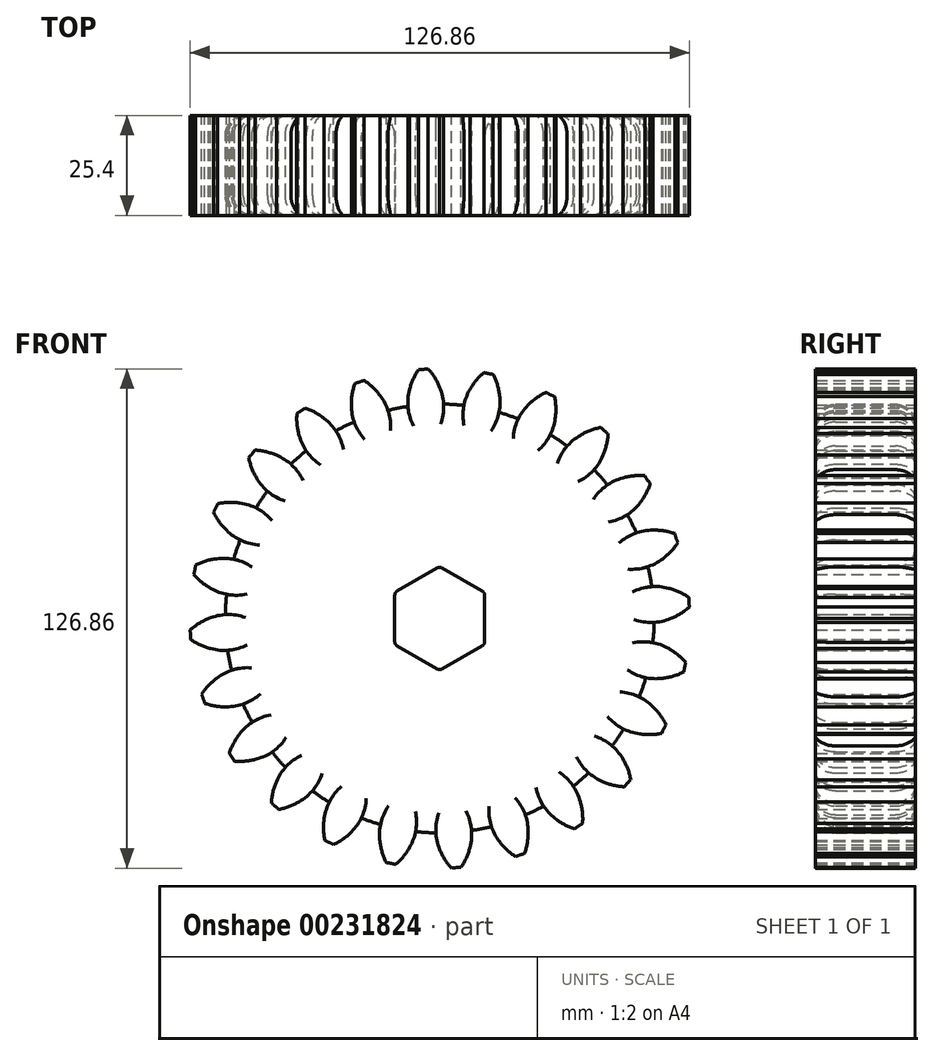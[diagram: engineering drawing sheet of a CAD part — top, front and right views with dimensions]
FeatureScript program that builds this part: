
annotation { "Feature Type Name" : "Feature", "Feature Type Description" : "" }
export const myFeature = defineFeature(function(context is Context, id is Id, definition is map)
    precondition{}
    {
        {
            var Q0;
            Q0=qCreatedBy(makeId("Front.planeOp"),FACE);
            var sketch = newSketch(context, id + "F0", { "sketchPlane" : qUnion([Q0])});
            skCircle(sketch, "E0", {"center": v(0, 0) * mm, "radius": 63.5 * mm, "construction": true});
            skCircle(sketch, "E1", {"center": v(0, 0) * mm, "radius": 58.67 * mm, "construction": true});
            skCircle(sketch, "E2", {"center": v(0, 0) * mm, "radius": 53.72 * mm});
            skLineSegment(sketch, "E3", {"start": v(0, 0) * mm, "end": v(0, 146.74) * mm, "construction": true});
            skLineSegment(sketch, "E4", {"start": v(0, 0) * mm, "end": v(-9.9, 151.07) * mm, "construction": true});
            skLineSegment(sketch, "E5", {"start": v(0, 58.67) * mm, "end": v(-143.25, 58.67) * mm, "construction": true});
            skLineSegment(sketch, "E6", {"start": v(0, 58.67) * mm, "end": v(-135.03, 9.53) * mm, "construction": true});
            skCircle(sketch, "E7", {"center": v(0, 0) * mm, "radius": 55.14 * mm, "construction": true});
            skCircle(sketch, "E8", {"center": v(0, 58.67) * mm, "radius": 14.6 * mm, "construction": true});
            skCircle(sketch, "E9", {"center": v(-13.63, 53.42) * mm, "radius": 14.64 * mm, "construction": true});
            skArc(sketch, "E10", {"start": v(0, 58.67) * mm, "mid": v(-1.26, 61.19) * mm, "end": v(-2.95, 63.43) * mm});
            skArc(sketch, "E11", {"start": v(1, 53.71) * mm, "mid": v(0.75, 56.24) * mm, "end": v(0, 58.67) * mm});
            skArc(sketch, "E12.MirrorCS", {"start": v(-7.66, 58.17) * mm, "mid": v(-6.74, 60.83) * mm, "end": v(-5.36, 63.27) * mm});
            skArc(sketch, "E13", {"start": v(-5.36, 63.27) * mm, "mid": v(-4.15, 63.3) * mm, "end": v(-2.95, 63.43) * mm});
            skArc(sketch, "E14.MirrorCS", {"start": v(-8, 53.12) * mm, "mid": v(-8.08, 55.66) * mm, "end": v(-7.66, 58.17) * mm});
            skSolve(sketch);
        }
        {
            var Q0;
            {var subQ0=sQuery(id+"F0.wireOp",EDGE,"E2");var subQ1=makeQuery(id+"F0.imprint","INTERSECT",VERTEX,{"derivedFrom":[subQ0,sQuery(id+"F0.wireOp",EDGE,"E11")]});Q0=makeQuery(id+"F0.imprint","IMPRINT",FACE,{"disambiguationData":[TD([[makeQuery(id+"F0.imprint","IMPRINT",EDGE,{"disambiguationData":[TD([[subQ1,-1.0]])],"derivedFrom":subQ0}),1.0]])]});}
            var Q1;
            Q1=makeQuery(id+"F0.imprint","IMPRINT",FACE,{"disambiguationData":[TD([[makeQuery(id+"F0.imprint","IMPRINT",EDGE,{"derivedFrom":sQuery(id+"F0.wireOp",EDGE,"E10")}),1.0]])]});
            extrude(context, id + "F1", {"entities" : qUnion([Q0, Q1]), "depth" : 25.4 * mm});
        }
        {
            var Q0;
            Q0=makeQuery(id+"F1.opExtrude","SWEPT_BODY",BODY,{"disambiguationData":[OSD([sQuery(id+"F0.wireOp",EDGE,"E2"),sQuery(id+"F0.wireOp",EDGE,"E10"),sQuery(id+"F0.wireOp",EDGE,"E11"),sQuery(id+"F0.wireOp",EDGE,"E12.MirrorCS"),sQuery(id+"F0.wireOp",EDGE,"E13"),sQuery(id+"F0.wireOp",EDGE,"E14.MirrorCS")])]});
            var Q1;
            Q1=makeQuery(id+"F1.opExtrude","SWEPT_FACE",FACE,{"disambiguationData":[OSD([sQuery(id+"F0.wireOp",EDGE,"E2")])]});
            circularPattern(context, id + "F2", {"entities" : qUnion([Q0]), "axis" : qUnion([Q1]), "angle" : 15 * degree, "instanceCount" : 24});
        }
        {
            var Q0;
            Q0=makeQuery(id+"F2.opPattern","COPY",FACE,{"derivedFrom":makeQuery(id+"F1.opExtrude","CAP_FACE",FACE,{"disambiguationData":[OSD([sQuery(id+"F0.wireOp",EDGE,"E2"),sQuery(id+"F0.wireOp",EDGE,"E10"),sQuery(id+"F0.wireOp",EDGE,"E11"),sQuery(id+"F0.wireOp",EDGE,"E12.MirrorCS"),sQuery(id+"F0.wireOp",EDGE,"E13"),sQuery(id+"F0.wireOp",EDGE,"E14.MirrorCS")])],"isStart":true}),"instanceName":"12"});
            var sketch = newSketch(context, id + "F3", { "sketchPlane" : qUnion([Q0])});
            skCircle(sketch, "E15", {"center": v(0, 0) * mm, "radius": 54.48 * mm});
            skSolve(sketch);
        }
        {
            var Q0;
            Q0 = qSketchRegion(id + "F3", true);
            extrude(context, id + "F4", {"entities" : qUnion([Q0]), "operationType" : NewBodyOperationType.ADD, "oppositeDirection" : true, "depth" : 25.4 * mm});
        }
        {
            var Q0;
            {var subQ0=makeQuery(id+"F1.opExtrude","CAP_FACE",FACE,{"disambiguationData":[OSD([sQuery(id+"F0.wireOp",EDGE,"E2"),sQuery(id+"F0.wireOp",EDGE,"E10"),sQuery(id+"F0.wireOp",EDGE,"E11"),sQuery(id+"F0.wireOp",EDGE,"E12.MirrorCS"),sQuery(id+"F0.wireOp",EDGE,"E13"),sQuery(id+"F0.wireOp",EDGE,"E14.MirrorCS")])],"isStart":false});Q0=makeQuery(id+"F4.boolean.opBoolean","MERGE",FACE,{"derivedFrom":[subQ0,makeQuery(id+"F2.opPattern","COPY",FACE,{"derivedFrom":subQ0,"instanceName":"1"}),makeQuery(id+"F2.opPattern","COPY",FACE,{"derivedFrom":subQ0,"instanceName":"2"}),makeQuery(id+"F2.opPattern","COPY",FACE,{"derivedFrom":subQ0,"instanceName":"3"}),makeQuery(id+"F2.opPattern","COPY",FACE,{"derivedFrom":subQ0,"instanceName":"4"}),makeQuery(id+"F2.opPattern","COPY",FACE,{"derivedFrom":subQ0,"instanceName":"5"}),makeQuery(id+"F2.opPattern","COPY",FACE,{"derivedFrom":subQ0,"instanceName":"6"}),makeQuery(id+"F2.opPattern","COPY",FACE,{"derivedFrom":subQ0,"instanceName":"7"}),makeQuery(id+"F2.opPattern","COPY",FACE,{"derivedFrom":subQ0,"instanceName":"8"}),makeQuery(id+"F2.opPattern","COPY",FACE,{"derivedFrom":subQ0,"instanceName":"9"}),makeQuery(id+"F2.opPattern","COPY",FACE,{"derivedFrom":subQ0,"instanceName":"10"}),makeQuery(id+"F2.opPattern","COPY",FACE,{"derivedFrom":subQ0,"instanceName":"11"}),makeQuery(id+"F2.opPattern","COPY",FACE,{"derivedFrom":subQ0,"instanceName":"12"}),makeQuery(id+"F2.opPattern","COPY",FACE,{"derivedFrom":subQ0,"instanceName":"13"}),makeQuery(id+"F2.opPattern","COPY",FACE,{"derivedFrom":subQ0,"instanceName":"14"}),makeQuery(id+"F2.opPattern","COPY",FACE,{"derivedFrom":subQ0,"instanceName":"15"}),makeQuery(id+"F2.opPattern","COPY",FACE,{"derivedFrom":subQ0,"instanceName":"16"}),makeQuery(id+"F2.opPattern","COPY",FACE,{"derivedFrom":subQ0,"instanceName":"17"}),makeQuery(id+"F2.opPattern","COPY",FACE,{"derivedFrom":subQ0,"instanceName":"18"}),makeQuery(id+"F2.opPattern","COPY",FACE,{"derivedFrom":subQ0,"instanceName":"19"}),makeQuery(id+"F2.opPattern","COPY",FACE,{"derivedFrom":subQ0,"instanceName":"20"}),makeQuery(id+"F2.opPattern","COPY",FACE,{"derivedFrom":subQ0,"instanceName":"21"}),makeQuery(id+"F2.opPattern","COPY",FACE,{"derivedFrom":subQ0,"instanceName":"22"}),makeQuery(id+"F2.opPattern","COPY",FACE,{"derivedFrom":subQ0,"instanceName":"23"}),makeQuery(id+"F4.opExtrude","CAP_FACE",FACE,{"disambiguationData":[OSD([sQuery(id+"F3.wireOp",EDGE,"E15")])],"isStart":false})]});}
            var sketch = newSketch(context, id + "F5", { "sketchPlane" : qUnion([Q0])});
            skCircle(sketch, "E16.cCircle", {"center": v(0, 0) * mm, "radius": 11.43 * mm, "construction": true});
            skLineSegment(sketch, "E16.0", {"start": v(11.43, -6.6) * mm, "end": v(0, -13.2) * mm});
            skLineSegment(sketch, "E16.1", {"start": v(0, -13.2) * mm, "end": v(-11.43, -6.6) * mm});
            skLineSegment(sketch, "E16.2", {"start": v(-11.43, -6.6) * mm, "end": v(-11.43, 6.6) * mm});
            skLineSegment(sketch, "E16.3", {"start": v(-11.43, 6.6) * mm, "end": v(0, 13.2) * mm});
            skLineSegment(sketch, "E16.4", {"start": v(0, 13.2) * mm, "end": v(11.43, 6.6) * mm});
            skLineSegment(sketch, "E16.5", {"start": v(11.43, 6.6) * mm, "end": v(11.43, -6.6) * mm});
            skPoint(sketch, "E16.0.midPoint", {"position": v(5.71, -9.9) * mm});
            skSolve(sketch);
        }
        {
            var Q0;
            Q0 = qSketchRegion(id + "F5", true);
            extrude(context, id + "F6", {"entities" : qUnion([Q0]), "operationType" : NewBodyOperationType.REMOVE, "oppositeDirection" : true, "depth" : 29.46 * mm});
        }
        {
            var Q0;
            Q0=makeQuery(id+"F6.boolean.opBoolean","COPY",EDGE,{"derivedFrom":makeQuery(id+"F6.opExtrude","SWEPT_EDGE",EDGE,{"disambiguationData":[OSD([sQuery(id+"F5.wireOp",EDGE,"E16.2"),sQuery(id+"F5.wireOp",EDGE,"E16.3")])]})});
            var Q1;
            Q1=makeQuery(id+"F6.boolean.opBoolean","COPY",EDGE,{"derivedFrom":makeQuery(id+"F6.opExtrude","SWEPT_EDGE",EDGE,{"disambiguationData":[OSD([sQuery(id+"F5.wireOp",EDGE,"E16.3"),sQuery(id+"F5.wireOp",EDGE,"E16.4")])]})});
            var Q2;
            Q2=makeQuery(id+"F6.boolean.opBoolean","COPY",EDGE,{"derivedFrom":makeQuery(id+"F6.opExtrude","SWEPT_EDGE",EDGE,{"disambiguationData":[OSD([sQuery(id+"F5.wireOp",EDGE,"E16.4"),sQuery(id+"F5.wireOp",EDGE,"E16.5")])]})});
            var Q3;
            Q3=makeQuery(id+"F6.boolean.opBoolean","COPY",EDGE,{"derivedFrom":makeQuery(id+"F6.opExtrude","SWEPT_EDGE",EDGE,{"disambiguationData":[OSD([sQuery(id+"F5.wireOp",EDGE,"E16.0"),sQuery(id+"F5.wireOp",EDGE,"E16.5")])]})});
            var Q4;
            Q4=makeQuery(id+"F6.boolean.opBoolean","COPY",EDGE,{"derivedFrom":makeQuery(id+"F6.opExtrude","SWEPT_EDGE",EDGE,{"disambiguationData":[OSD([sQuery(id+"F5.wireOp",EDGE,"E16.0"),sQuery(id+"F5.wireOp",EDGE,"E16.1")])]})});
            var Q5;
            Q5=makeQuery(id+"F6.boolean.opBoolean","COPY",EDGE,{"derivedFrom":makeQuery(id+"F6.opExtrude","SWEPT_EDGE",EDGE,{"disambiguationData":[OSD([sQuery(id+"F5.wireOp",EDGE,"E16.1"),sQuery(id+"F5.wireOp",EDGE,"E16.2")])]})});
            fillet(context, id + "F7", {"entities" : qUnion([Q0, Q1, Q2, Q3, Q4, Q5]), "radius" : 1.27 * mm, "tangentPropagation" : true, "allowEdgeOverflow" : false});
        }
        {
            var Q0;
            Q0=makeQuery(id+"F6.boolean.opBoolean","COPY",EDGE,{"derivedFrom":makeQuery(id+"F6.opExtrude","CAP_EDGE",EDGE,{"disambiguationData":[OSD([sQuery(id+"F5.wireOp",EDGE,"E16.3")])],"isStart":true})});
            var Q1;
            {var subQ0=makeQuery(id+"F1.opExtrude","CAP_FACE",FACE,{"disambiguationData":[OSD([sQuery(id+"F0.wireOp",EDGE,"E2"),sQuery(id+"F0.wireOp",EDGE,"E10"),sQuery(id+"F0.wireOp",EDGE,"E11"),sQuery(id+"F0.wireOp",EDGE,"E12.MirrorCS"),sQuery(id+"F0.wireOp",EDGE,"E13"),sQuery(id+"F0.wireOp",EDGE,"E14.MirrorCS")])],"isStart":true});Q1=makeQuery(id+"F6.boolean.opBoolean","INTERSECT",EDGE,{"derivedFrom":[makeQuery(id+"F4.boolean.opBoolean","MERGE",FACE,{"derivedFrom":[subQ0,makeQuery(id+"F2.opPattern","COPY",FACE,{"derivedFrom":subQ0,"instanceName":"1"}),makeQuery(id+"F2.opPattern","COPY",FACE,{"derivedFrom":subQ0,"instanceName":"2"}),makeQuery(id+"F2.opPattern","COPY",FACE,{"derivedFrom":subQ0,"instanceName":"3"}),makeQuery(id+"F2.opPattern","COPY",FACE,{"derivedFrom":subQ0,"instanceName":"4"}),makeQuery(id+"F2.opPattern","COPY",FACE,{"derivedFrom":subQ0,"instanceName":"5"}),makeQuery(id+"F2.opPattern","COPY",FACE,{"derivedFrom":subQ0,"instanceName":"6"}),makeQuery(id+"F2.opPattern","COPY",FACE,{"derivedFrom":subQ0,"instanceName":"7"}),makeQuery(id+"F2.opPattern","COPY",FACE,{"derivedFrom":subQ0,"instanceName":"8"}),makeQuery(id+"F2.opPattern","COPY",FACE,{"derivedFrom":subQ0,"instanceName":"9"}),makeQuery(id+"F2.opPattern","COPY",FACE,{"derivedFrom":subQ0,"instanceName":"10"}),makeQuery(id+"F2.opPattern","COPY",FACE,{"derivedFrom":subQ0,"instanceName":"11"}),makeQuery(id+"F2.opPattern","COPY",FACE,{"derivedFrom":subQ0,"instanceName":"12"}),makeQuery(id+"F2.opPattern","COPY",FACE,{"derivedFrom":subQ0,"instanceName":"13"}),makeQuery(id+"F2.opPattern","COPY",FACE,{"derivedFrom":subQ0,"instanceName":"14"}),makeQuery(id+"F2.opPattern","COPY",FACE,{"derivedFrom":subQ0,"instanceName":"15"}),makeQuery(id+"F2.opPattern","COPY",FACE,{"derivedFrom":subQ0,"instanceName":"16"}),makeQuery(id+"F2.opPattern","COPY",FACE,{"derivedFrom":subQ0,"instanceName":"17"}),makeQuery(id+"F2.opPattern","COPY",FACE,{"derivedFrom":subQ0,"instanceName":"18"}),makeQuery(id+"F2.opPattern","COPY",FACE,{"derivedFrom":subQ0,"instanceName":"19"}),makeQuery(id+"F2.opPattern","COPY",FACE,{"derivedFrom":subQ0,"instanceName":"20"}),makeQuery(id+"F2.opPattern","COPY",FACE,{"derivedFrom":subQ0,"instanceName":"21"}),makeQuery(id+"F2.opPattern","COPY",FACE,{"derivedFrom":subQ0,"instanceName":"22"}),makeQuery(id+"F2.opPattern","COPY",FACE,{"derivedFrom":subQ0,"instanceName":"23"}),makeQuery(id+"F4.opExtrude","CAP_FACE",FACE,{"disambiguationData":[OSD([sQuery(id+"F3.wireOp",EDGE,"E15")])],"isStart":true})]}),makeQuery(id+"F6.opExtrude","SWEPT_FACE",FACE,{"disambiguationData":[OSD([sQuery(id+"F5.wireOp",EDGE,"E16.4")])]})]});}
            fillet(context, id + "F8", {"entities" : qUnion([Q0, Q1]), "radius" : 5.08 * mm, "tangentPropagation" : true, "allowEdgeOverflow" : false});
        }
        {
            var Q0;
            {var subQ1=sQuery(id+"F0.wireOp",EDGE,"E11");var subQ3=sQuery(id+"F3.wireOp",EDGE,"E15");Q0=makeQuery(id+"F4.boolean.opBoolean","SPLIT",EDGE,{"disambiguationData":[TD([makeQuery(id+"F1.opExtrude","SWEPT_FACE",FACE,{"disambiguationData":[OSD([subQ1])]})])],"derivedFrom":makeQuery(id+"F4.opExtrude","CAP_EDGE",EDGE,{"disambiguationData":[OSD([subQ3])],"isStart":true})});}
            var Q1;
            {var subQ0=sQuery(id+"F0.wireOp",EDGE,"E14.MirrorCS");var subQ3=sQuery(id+"F3.wireOp",EDGE,"E15");Q1=makeQuery(id+"F4.boolean.opBoolean","SPLIT",EDGE,{"disambiguationData":[TD([makeQuery(id+"F1.opExtrude","SWEPT_FACE",FACE,{"disambiguationData":[OSD([subQ0])]})])],"derivedFrom":makeQuery(id+"F4.opExtrude","CAP_EDGE",EDGE,{"disambiguationData":[OSD([subQ3])],"isStart":true})});}
            var Q2;
            {var subQ1=sQuery(id+"F0.wireOp",EDGE,"E11");var subQ3=sQuery(id+"F3.wireOp",EDGE,"E15");Q2=makeQuery(id+"F4.boolean.opBoolean","SPLIT",EDGE,{"disambiguationData":[TD([makeQuery(id+"F2.opPattern","COPY",FACE,{"derivedFrom":makeQuery(id+"F1.opExtrude","SWEPT_FACE",FACE,{"disambiguationData":[OSD([subQ1])]}),"instanceName":"22"})])],"derivedFrom":makeQuery(id+"F4.opExtrude","CAP_EDGE",EDGE,{"disambiguationData":[OSD([subQ3])],"isStart":true})});}
            var Q3;
            {var subQ1=sQuery(id+"F0.wireOp",EDGE,"E11");var subQ3=sQuery(id+"F3.wireOp",EDGE,"E15");Q3=makeQuery(id+"F4.boolean.opBoolean","SPLIT",EDGE,{"disambiguationData":[TD([makeQuery(id+"F2.opPattern","COPY",FACE,{"derivedFrom":makeQuery(id+"F1.opExtrude","SWEPT_FACE",FACE,{"disambiguationData":[OSD([subQ1])]}),"instanceName":"21"})])],"derivedFrom":makeQuery(id+"F4.opExtrude","CAP_EDGE",EDGE,{"disambiguationData":[OSD([subQ3])],"isStart":true})});}
            var Q4;
            {var subQ1=sQuery(id+"F0.wireOp",EDGE,"E11");var subQ3=sQuery(id+"F3.wireOp",EDGE,"E15");Q4=makeQuery(id+"F4.boolean.opBoolean","SPLIT",EDGE,{"disambiguationData":[TD([makeQuery(id+"F2.opPattern","COPY",FACE,{"derivedFrom":makeQuery(id+"F1.opExtrude","SWEPT_FACE",FACE,{"disambiguationData":[OSD([subQ1])]}),"instanceName":"20"})])],"derivedFrom":makeQuery(id+"F4.opExtrude","CAP_EDGE",EDGE,{"disambiguationData":[OSD([subQ3])],"isStart":true})});}
            var Q5;
            {var subQ1=sQuery(id+"F0.wireOp",EDGE,"E11");var subQ3=sQuery(id+"F3.wireOp",EDGE,"E15");Q5=makeQuery(id+"F4.boolean.opBoolean","SPLIT",EDGE,{"disambiguationData":[TD([makeQuery(id+"F2.opPattern","COPY",FACE,{"derivedFrom":makeQuery(id+"F1.opExtrude","SWEPT_FACE",FACE,{"disambiguationData":[OSD([subQ1])]}),"instanceName":"19"})])],"derivedFrom":makeQuery(id+"F4.opExtrude","CAP_EDGE",EDGE,{"disambiguationData":[OSD([subQ3])],"isStart":true})});}
            var Q6;
            {var subQ1=sQuery(id+"F0.wireOp",EDGE,"E11");var subQ3=sQuery(id+"F3.wireOp",EDGE,"E15");Q6=makeQuery(id+"F4.boolean.opBoolean","SPLIT",EDGE,{"disambiguationData":[TD([makeQuery(id+"F2.opPattern","COPY",FACE,{"derivedFrom":makeQuery(id+"F1.opExtrude","SWEPT_FACE",FACE,{"disambiguationData":[OSD([subQ1])]}),"instanceName":"18"})])],"derivedFrom":makeQuery(id+"F4.opExtrude","CAP_EDGE",EDGE,{"disambiguationData":[OSD([subQ3])],"isStart":true})});}
            var Q7;
            {var subQ1=sQuery(id+"F0.wireOp",EDGE,"E11");var subQ3=sQuery(id+"F3.wireOp",EDGE,"E15");Q7=makeQuery(id+"F4.boolean.opBoolean","SPLIT",EDGE,{"disambiguationData":[TD([makeQuery(id+"F2.opPattern","COPY",FACE,{"derivedFrom":makeQuery(id+"F1.opExtrude","SWEPT_FACE",FACE,{"disambiguationData":[OSD([subQ1])]}),"instanceName":"17"})])],"derivedFrom":makeQuery(id+"F4.opExtrude","CAP_EDGE",EDGE,{"disambiguationData":[OSD([subQ3])],"isStart":true})});}
            var Q8;
            {var subQ1=sQuery(id+"F0.wireOp",EDGE,"E11");var subQ3=sQuery(id+"F3.wireOp",EDGE,"E15");Q8=makeQuery(id+"F4.boolean.opBoolean","SPLIT",EDGE,{"disambiguationData":[TD([makeQuery(id+"F2.opPattern","COPY",FACE,{"derivedFrom":makeQuery(id+"F1.opExtrude","SWEPT_FACE",FACE,{"disambiguationData":[OSD([subQ1])]}),"instanceName":"16"})])],"derivedFrom":makeQuery(id+"F4.opExtrude","CAP_EDGE",EDGE,{"disambiguationData":[OSD([subQ3])],"isStart":true})});}
            var Q9;
            {var subQ1=sQuery(id+"F0.wireOp",EDGE,"E11");var subQ3=sQuery(id+"F3.wireOp",EDGE,"E15");Q9=makeQuery(id+"F4.boolean.opBoolean","SPLIT",EDGE,{"disambiguationData":[TD([makeQuery(id+"F2.opPattern","COPY",FACE,{"derivedFrom":makeQuery(id+"F1.opExtrude","SWEPT_FACE",FACE,{"disambiguationData":[OSD([subQ1])]}),"instanceName":"15"})])],"derivedFrom":makeQuery(id+"F4.opExtrude","CAP_EDGE",EDGE,{"disambiguationData":[OSD([subQ3])],"isStart":true})});}
            var Q10;
            {var subQ1=sQuery(id+"F0.wireOp",EDGE,"E11");var subQ3=sQuery(id+"F3.wireOp",EDGE,"E15");Q10=makeQuery(id+"F4.boolean.opBoolean","SPLIT",EDGE,{"disambiguationData":[TD([makeQuery(id+"F2.opPattern","COPY",FACE,{"derivedFrom":makeQuery(id+"F1.opExtrude","SWEPT_FACE",FACE,{"disambiguationData":[OSD([subQ1])]}),"instanceName":"14"})])],"derivedFrom":makeQuery(id+"F4.opExtrude","CAP_EDGE",EDGE,{"disambiguationData":[OSD([subQ3])],"isStart":true})});}
            var Q11;
            {var subQ1=sQuery(id+"F0.wireOp",EDGE,"E11");var subQ3=sQuery(id+"F3.wireOp",EDGE,"E15");Q11=makeQuery(id+"F4.boolean.opBoolean","SPLIT",EDGE,{"disambiguationData":[TD([makeQuery(id+"F2.opPattern","COPY",FACE,{"derivedFrom":makeQuery(id+"F1.opExtrude","SWEPT_FACE",FACE,{"disambiguationData":[OSD([subQ1])]}),"instanceName":"13"})])],"derivedFrom":makeQuery(id+"F4.opExtrude","CAP_EDGE",EDGE,{"disambiguationData":[OSD([subQ3])],"isStart":true})});}
            var Q12;
            {var subQ1=sQuery(id+"F0.wireOp",EDGE,"E11");var subQ3=sQuery(id+"F3.wireOp",EDGE,"E15");Q12=makeQuery(id+"F4.boolean.opBoolean","SPLIT",EDGE,{"disambiguationData":[TD([makeQuery(id+"F2.opPattern","COPY",FACE,{"derivedFrom":makeQuery(id+"F1.opExtrude","SWEPT_FACE",FACE,{"disambiguationData":[OSD([subQ1])]}),"instanceName":"12"})])],"derivedFrom":makeQuery(id+"F4.opExtrude","CAP_EDGE",EDGE,{"disambiguationData":[OSD([subQ3])],"isStart":true})});}
            var Q13;
            {var subQ1=sQuery(id+"F0.wireOp",EDGE,"E11");var subQ3=sQuery(id+"F3.wireOp",EDGE,"E15");Q13=makeQuery(id+"F4.boolean.opBoolean","SPLIT",EDGE,{"disambiguationData":[TD([makeQuery(id+"F2.opPattern","COPY",FACE,{"derivedFrom":makeQuery(id+"F1.opExtrude","SWEPT_FACE",FACE,{"disambiguationData":[OSD([subQ1])]}),"instanceName":"11"})])],"derivedFrom":makeQuery(id+"F4.opExtrude","CAP_EDGE",EDGE,{"disambiguationData":[OSD([subQ3])],"isStart":true})});}
            var Q14;
            {var subQ1=sQuery(id+"F0.wireOp",EDGE,"E11");var subQ3=sQuery(id+"F3.wireOp",EDGE,"E15");Q14=makeQuery(id+"F4.boolean.opBoolean","SPLIT",EDGE,{"disambiguationData":[TD([makeQuery(id+"F2.opPattern","COPY",FACE,{"derivedFrom":makeQuery(id+"F1.opExtrude","SWEPT_FACE",FACE,{"disambiguationData":[OSD([subQ1])]}),"instanceName":"10"})])],"derivedFrom":makeQuery(id+"F4.opExtrude","CAP_EDGE",EDGE,{"disambiguationData":[OSD([subQ3])],"isStart":true})});}
            var Q15;
            {var subQ1=sQuery(id+"F0.wireOp",EDGE,"E11");var subQ3=sQuery(id+"F3.wireOp",EDGE,"E15");Q15=makeQuery(id+"F4.boolean.opBoolean","SPLIT",EDGE,{"disambiguationData":[TD([makeQuery(id+"F2.opPattern","COPY",FACE,{"derivedFrom":makeQuery(id+"F1.opExtrude","SWEPT_FACE",FACE,{"disambiguationData":[OSD([subQ1])]}),"instanceName":"9"})])],"derivedFrom":makeQuery(id+"F4.opExtrude","CAP_EDGE",EDGE,{"disambiguationData":[OSD([subQ3])],"isStart":true})});}
            var Q16;
            {var subQ1=sQuery(id+"F0.wireOp",EDGE,"E11");var subQ3=sQuery(id+"F3.wireOp",EDGE,"E15");Q16=makeQuery(id+"F4.boolean.opBoolean","SPLIT",EDGE,{"disambiguationData":[TD([makeQuery(id+"F2.opPattern","COPY",FACE,{"derivedFrom":makeQuery(id+"F1.opExtrude","SWEPT_FACE",FACE,{"disambiguationData":[OSD([subQ1])]}),"instanceName":"8"})])],"derivedFrom":makeQuery(id+"F4.opExtrude","CAP_EDGE",EDGE,{"disambiguationData":[OSD([subQ3])],"isStart":true})});}
            var Q17;
            {var subQ1=sQuery(id+"F0.wireOp",EDGE,"E11");var subQ3=sQuery(id+"F3.wireOp",EDGE,"E15");Q17=makeQuery(id+"F4.boolean.opBoolean","SPLIT",EDGE,{"disambiguationData":[TD([makeQuery(id+"F2.opPattern","COPY",FACE,{"derivedFrom":makeQuery(id+"F1.opExtrude","SWEPT_FACE",FACE,{"disambiguationData":[OSD([subQ1])]}),"instanceName":"7"})])],"derivedFrom":makeQuery(id+"F4.opExtrude","CAP_EDGE",EDGE,{"disambiguationData":[OSD([subQ3])],"isStart":true})});}
            var Q18;
            {var subQ1=sQuery(id+"F0.wireOp",EDGE,"E11");var subQ3=sQuery(id+"F3.wireOp",EDGE,"E15");Q18=makeQuery(id+"F4.boolean.opBoolean","SPLIT",EDGE,{"disambiguationData":[TD([makeQuery(id+"F2.opPattern","COPY",FACE,{"derivedFrom":makeQuery(id+"F1.opExtrude","SWEPT_FACE",FACE,{"disambiguationData":[OSD([subQ1])]}),"instanceName":"6"})])],"derivedFrom":makeQuery(id+"F4.opExtrude","CAP_EDGE",EDGE,{"disambiguationData":[OSD([subQ3])],"isStart":true})});}
            var Q19;
            {var subQ1=sQuery(id+"F0.wireOp",EDGE,"E11");var subQ3=sQuery(id+"F3.wireOp",EDGE,"E15");Q19=makeQuery(id+"F4.boolean.opBoolean","SPLIT",EDGE,{"disambiguationData":[TD([makeQuery(id+"F2.opPattern","COPY",FACE,{"derivedFrom":makeQuery(id+"F1.opExtrude","SWEPT_FACE",FACE,{"disambiguationData":[OSD([subQ1])]}),"instanceName":"5"})])],"derivedFrom":makeQuery(id+"F4.opExtrude","CAP_EDGE",EDGE,{"disambiguationData":[OSD([subQ3])],"isStart":true})});}
            var Q20;
            {var subQ1=sQuery(id+"F0.wireOp",EDGE,"E11");var subQ3=sQuery(id+"F3.wireOp",EDGE,"E15");Q20=makeQuery(id+"F4.boolean.opBoolean","SPLIT",EDGE,{"disambiguationData":[TD([makeQuery(id+"F2.opPattern","COPY",FACE,{"derivedFrom":makeQuery(id+"F1.opExtrude","SWEPT_FACE",FACE,{"disambiguationData":[OSD([subQ1])]}),"instanceName":"4"})])],"derivedFrom":makeQuery(id+"F4.opExtrude","CAP_EDGE",EDGE,{"disambiguationData":[OSD([subQ3])],"isStart":true})});}
            var Q21;
            {var subQ1=sQuery(id+"F0.wireOp",EDGE,"E11");var subQ3=sQuery(id+"F3.wireOp",EDGE,"E15");Q21=makeQuery(id+"F4.boolean.opBoolean","SPLIT",EDGE,{"disambiguationData":[TD([makeQuery(id+"F2.opPattern","COPY",FACE,{"derivedFrom":makeQuery(id+"F1.opExtrude","SWEPT_FACE",FACE,{"disambiguationData":[OSD([subQ1])]}),"instanceName":"3"})])],"derivedFrom":makeQuery(id+"F4.opExtrude","CAP_EDGE",EDGE,{"disambiguationData":[OSD([subQ3])],"isStart":true})});}
            var Q22;
            {var subQ1=sQuery(id+"F0.wireOp",EDGE,"E11");var subQ3=sQuery(id+"F3.wireOp",EDGE,"E15");Q22=makeQuery(id+"F4.boolean.opBoolean","SPLIT",EDGE,{"disambiguationData":[TD([makeQuery(id+"F2.opPattern","COPY",FACE,{"derivedFrom":makeQuery(id+"F1.opExtrude","SWEPT_FACE",FACE,{"disambiguationData":[OSD([subQ1])]}),"instanceName":"2"})])],"derivedFrom":makeQuery(id+"F4.opExtrude","CAP_EDGE",EDGE,{"disambiguationData":[OSD([subQ3])],"isStart":true})});}
            var Q23;
            {var subQ1=sQuery(id+"F0.wireOp",EDGE,"E11");var subQ3=sQuery(id+"F3.wireOp",EDGE,"E15");Q23=makeQuery(id+"F4.boolean.opBoolean","SPLIT",EDGE,{"disambiguationData":[TD([makeQuery(id+"F2.opPattern","COPY",FACE,{"derivedFrom":makeQuery(id+"F1.opExtrude","SWEPT_FACE",FACE,{"disambiguationData":[OSD([subQ1])]}),"instanceName":"1"})])],"derivedFrom":makeQuery(id+"F4.opExtrude","CAP_EDGE",EDGE,{"disambiguationData":[OSD([subQ3])],"isStart":true})});}
            var Q24;
            {var subQ1=sQuery(id+"F0.wireOp",EDGE,"E11");var subQ3=sQuery(id+"F3.wireOp",EDGE,"E15");Q24=makeQuery(id+"F4.boolean.opBoolean","SPLIT",EDGE,{"disambiguationData":[TD([makeQuery(id+"F2.opPattern","COPY",FACE,{"derivedFrom":makeQuery(id+"F1.opExtrude","SWEPT_FACE",FACE,{"disambiguationData":[OSD([subQ1])]}),"instanceName":"19"})])],"derivedFrom":makeQuery(id+"F4.opExtrude","CAP_EDGE",EDGE,{"disambiguationData":[OSD([subQ3])],"isStart":false})});}
            var Q25;
            {var subQ0=sQuery(id+"F0.wireOp",EDGE,"E11");var subQ3=sQuery(id+"F3.wireOp",EDGE,"E15");Q25=makeQuery(id+"F4.boolean.opBoolean","SPLIT",EDGE,{"disambiguationData":[TD([makeQuery(id+"F2.opPattern","COPY",FACE,{"derivedFrom":makeQuery(id+"F1.opExtrude","SWEPT_FACE",FACE,{"disambiguationData":[OSD([subQ0])]}),"instanceName":"20"})])],"derivedFrom":makeQuery(id+"F4.opExtrude","CAP_EDGE",EDGE,{"disambiguationData":[OSD([subQ3])],"isStart":false})});}
            var Q26;
            {var subQ1=sQuery(id+"F0.wireOp",EDGE,"E11");var subQ3=sQuery(id+"F3.wireOp",EDGE,"E15");Q26=makeQuery(id+"F4.boolean.opBoolean","SPLIT",EDGE,{"disambiguationData":[TD([makeQuery(id+"F2.opPattern","COPY",FACE,{"derivedFrom":makeQuery(id+"F1.opExtrude","SWEPT_FACE",FACE,{"disambiguationData":[OSD([subQ1])]}),"instanceName":"21"})])],"derivedFrom":makeQuery(id+"F4.opExtrude","CAP_EDGE",EDGE,{"disambiguationData":[OSD([subQ3])],"isStart":false})});}
            var Q27;
            {var subQ1=sQuery(id+"F0.wireOp",EDGE,"E11");var subQ3=sQuery(id+"F3.wireOp",EDGE,"E15");Q27=makeQuery(id+"F4.boolean.opBoolean","SPLIT",EDGE,{"disambiguationData":[TD([makeQuery(id+"F2.opPattern","COPY",FACE,{"derivedFrom":makeQuery(id+"F1.opExtrude","SWEPT_FACE",FACE,{"disambiguationData":[OSD([subQ1])]}),"instanceName":"22"})])],"derivedFrom":makeQuery(id+"F4.opExtrude","CAP_EDGE",EDGE,{"disambiguationData":[OSD([subQ3])],"isStart":false})});}
            var Q28;
            {var subQ0=sQuery(id+"F0.wireOp",EDGE,"E14.MirrorCS");var subQ3=sQuery(id+"F3.wireOp",EDGE,"E15");Q28=makeQuery(id+"F4.boolean.opBoolean","SPLIT",EDGE,{"disambiguationData":[TD([makeQuery(id+"F1.opExtrude","SWEPT_FACE",FACE,{"disambiguationData":[OSD([subQ0])]})])],"derivedFrom":makeQuery(id+"F4.opExtrude","CAP_EDGE",EDGE,{"disambiguationData":[OSD([subQ3])],"isStart":false})});}
            var Q29;
            {var subQ1=sQuery(id+"F0.wireOp",EDGE,"E11");var subQ3=sQuery(id+"F3.wireOp",EDGE,"E15");Q29=makeQuery(id+"F4.boolean.opBoolean","SPLIT",EDGE,{"disambiguationData":[TD([makeQuery(id+"F2.opPattern","COPY",FACE,{"derivedFrom":makeQuery(id+"F1.opExtrude","SWEPT_FACE",FACE,{"disambiguationData":[OSD([subQ1])]}),"instanceName":"18"})])],"derivedFrom":makeQuery(id+"F4.opExtrude","CAP_EDGE",EDGE,{"disambiguationData":[OSD([subQ3])],"isStart":false})});}
            var Q30;
            {var subQ1=sQuery(id+"F0.wireOp",EDGE,"E11");var subQ3=sQuery(id+"F3.wireOp",EDGE,"E15");Q30=makeQuery(id+"F4.boolean.opBoolean","SPLIT",EDGE,{"disambiguationData":[TD([makeQuery(id+"F2.opPattern","COPY",FACE,{"derivedFrom":makeQuery(id+"F1.opExtrude","SWEPT_FACE",FACE,{"disambiguationData":[OSD([subQ1])]}),"instanceName":"17"})])],"derivedFrom":makeQuery(id+"F4.opExtrude","CAP_EDGE",EDGE,{"disambiguationData":[OSD([subQ3])],"isStart":false})});}
            var Q31;
            {var subQ1=sQuery(id+"F0.wireOp",EDGE,"E11");var subQ3=sQuery(id+"F3.wireOp",EDGE,"E15");Q31=makeQuery(id+"F4.boolean.opBoolean","SPLIT",EDGE,{"disambiguationData":[TD([makeQuery(id+"F2.opPattern","COPY",FACE,{"derivedFrom":makeQuery(id+"F1.opExtrude","SWEPT_FACE",FACE,{"disambiguationData":[OSD([subQ1])]}),"instanceName":"16"})])],"derivedFrom":makeQuery(id+"F4.opExtrude","CAP_EDGE",EDGE,{"disambiguationData":[OSD([subQ3])],"isStart":false})});}
            var Q32;
            {var subQ1=sQuery(id+"F0.wireOp",EDGE,"E11");var subQ3=sQuery(id+"F3.wireOp",EDGE,"E15");Q32=makeQuery(id+"F4.boolean.opBoolean","SPLIT",EDGE,{"disambiguationData":[TD([makeQuery(id+"F2.opPattern","COPY",FACE,{"derivedFrom":makeQuery(id+"F1.opExtrude","SWEPT_FACE",FACE,{"disambiguationData":[OSD([subQ1])]}),"instanceName":"15"})])],"derivedFrom":makeQuery(id+"F4.opExtrude","CAP_EDGE",EDGE,{"disambiguationData":[OSD([subQ3])],"isStart":false})});}
            var Q33;
            {var subQ1=sQuery(id+"F0.wireOp",EDGE,"E11");var subQ3=sQuery(id+"F3.wireOp",EDGE,"E15");Q33=makeQuery(id+"F4.boolean.opBoolean","SPLIT",EDGE,{"disambiguationData":[TD([makeQuery(id+"F2.opPattern","COPY",FACE,{"derivedFrom":makeQuery(id+"F1.opExtrude","SWEPT_FACE",FACE,{"disambiguationData":[OSD([subQ1])]}),"instanceName":"14"})])],"derivedFrom":makeQuery(id+"F4.opExtrude","CAP_EDGE",EDGE,{"disambiguationData":[OSD([subQ3])],"isStart":false})});}
            var Q34;
            {var subQ1=sQuery(id+"F0.wireOp",EDGE,"E11");var subQ3=sQuery(id+"F3.wireOp",EDGE,"E15");Q34=makeQuery(id+"F4.boolean.opBoolean","SPLIT",EDGE,{"disambiguationData":[TD([makeQuery(id+"F2.opPattern","COPY",FACE,{"derivedFrom":makeQuery(id+"F1.opExtrude","SWEPT_FACE",FACE,{"disambiguationData":[OSD([subQ1])]}),"instanceName":"13"})])],"derivedFrom":makeQuery(id+"F4.opExtrude","CAP_EDGE",EDGE,{"disambiguationData":[OSD([subQ3])],"isStart":false})});}
            var Q35;
            {var subQ1=sQuery(id+"F0.wireOp",EDGE,"E11");var subQ3=sQuery(id+"F3.wireOp",EDGE,"E15");Q35=makeQuery(id+"F4.boolean.opBoolean","SPLIT",EDGE,{"disambiguationData":[TD([makeQuery(id+"F2.opPattern","COPY",FACE,{"derivedFrom":makeQuery(id+"F1.opExtrude","SWEPT_FACE",FACE,{"disambiguationData":[OSD([subQ1])]}),"instanceName":"12"})])],"derivedFrom":makeQuery(id+"F4.opExtrude","CAP_EDGE",EDGE,{"disambiguationData":[OSD([subQ3])],"isStart":false})});}
            var Q36;
            {var subQ1=sQuery(id+"F0.wireOp",EDGE,"E11");var subQ3=sQuery(id+"F3.wireOp",EDGE,"E15");Q36=makeQuery(id+"F4.boolean.opBoolean","SPLIT",EDGE,{"disambiguationData":[TD([makeQuery(id+"F2.opPattern","COPY",FACE,{"derivedFrom":makeQuery(id+"F1.opExtrude","SWEPT_FACE",FACE,{"disambiguationData":[OSD([subQ1])]}),"instanceName":"11"})])],"derivedFrom":makeQuery(id+"F4.opExtrude","CAP_EDGE",EDGE,{"disambiguationData":[OSD([subQ3])],"isStart":false})});}
            var Q37;
            {var subQ1=sQuery(id+"F0.wireOp",EDGE,"E11");var subQ3=sQuery(id+"F3.wireOp",EDGE,"E15");Q37=makeQuery(id+"F4.boolean.opBoolean","SPLIT",EDGE,{"disambiguationData":[TD([makeQuery(id+"F2.opPattern","COPY",FACE,{"derivedFrom":makeQuery(id+"F1.opExtrude","SWEPT_FACE",FACE,{"disambiguationData":[OSD([subQ1])]}),"instanceName":"10"})])],"derivedFrom":makeQuery(id+"F4.opExtrude","CAP_EDGE",EDGE,{"disambiguationData":[OSD([subQ3])],"isStart":false})});}
            var Q38;
            {var subQ1=sQuery(id+"F0.wireOp",EDGE,"E11");var subQ3=sQuery(id+"F3.wireOp",EDGE,"E15");Q38=makeQuery(id+"F4.boolean.opBoolean","SPLIT",EDGE,{"disambiguationData":[TD([makeQuery(id+"F1.opExtrude","SWEPT_FACE",FACE,{"disambiguationData":[OSD([subQ1])]})])],"derivedFrom":makeQuery(id+"F4.opExtrude","CAP_EDGE",EDGE,{"disambiguationData":[OSD([subQ3])],"isStart":false})});}
            var Q39;
            {var subQ1=sQuery(id+"F0.wireOp",EDGE,"E11");var subQ3=sQuery(id+"F3.wireOp",EDGE,"E15");Q39=makeQuery(id+"F4.boolean.opBoolean","SPLIT",EDGE,{"disambiguationData":[TD([makeQuery(id+"F2.opPattern","COPY",FACE,{"derivedFrom":makeQuery(id+"F1.opExtrude","SWEPT_FACE",FACE,{"disambiguationData":[OSD([subQ1])]}),"instanceName":"1"})])],"derivedFrom":makeQuery(id+"F4.opExtrude","CAP_EDGE",EDGE,{"disambiguationData":[OSD([subQ3])],"isStart":false})});}
            var Q40;
            {var subQ1=sQuery(id+"F0.wireOp",EDGE,"E11");var subQ3=sQuery(id+"F3.wireOp",EDGE,"E15");Q40=makeQuery(id+"F4.boolean.opBoolean","SPLIT",EDGE,{"disambiguationData":[TD([makeQuery(id+"F2.opPattern","COPY",FACE,{"derivedFrom":makeQuery(id+"F1.opExtrude","SWEPT_FACE",FACE,{"disambiguationData":[OSD([subQ1])]}),"instanceName":"2"})])],"derivedFrom":makeQuery(id+"F4.opExtrude","CAP_EDGE",EDGE,{"disambiguationData":[OSD([subQ3])],"isStart":false})});}
            var Q41;
            {var subQ1=sQuery(id+"F0.wireOp",EDGE,"E11");var subQ3=sQuery(id+"F3.wireOp",EDGE,"E15");Q41=makeQuery(id+"F4.boolean.opBoolean","SPLIT",EDGE,{"disambiguationData":[TD([makeQuery(id+"F2.opPattern","COPY",FACE,{"derivedFrom":makeQuery(id+"F1.opExtrude","SWEPT_FACE",FACE,{"disambiguationData":[OSD([subQ1])]}),"instanceName":"3"})])],"derivedFrom":makeQuery(id+"F4.opExtrude","CAP_EDGE",EDGE,{"disambiguationData":[OSD([subQ3])],"isStart":false})});}
            var Q42;
            {var subQ1=sQuery(id+"F0.wireOp",EDGE,"E11");var subQ3=sQuery(id+"F3.wireOp",EDGE,"E15");Q42=makeQuery(id+"F4.boolean.opBoolean","SPLIT",EDGE,{"disambiguationData":[TD([makeQuery(id+"F2.opPattern","COPY",FACE,{"derivedFrom":makeQuery(id+"F1.opExtrude","SWEPT_FACE",FACE,{"disambiguationData":[OSD([subQ1])]}),"instanceName":"4"})])],"derivedFrom":makeQuery(id+"F4.opExtrude","CAP_EDGE",EDGE,{"disambiguationData":[OSD([subQ3])],"isStart":false})});}
            var Q43;
            {var subQ1=sQuery(id+"F0.wireOp",EDGE,"E11");var subQ3=sQuery(id+"F3.wireOp",EDGE,"E15");Q43=makeQuery(id+"F4.boolean.opBoolean","SPLIT",EDGE,{"disambiguationData":[TD([makeQuery(id+"F2.opPattern","COPY",FACE,{"derivedFrom":makeQuery(id+"F1.opExtrude","SWEPT_FACE",FACE,{"disambiguationData":[OSD([subQ1])]}),"instanceName":"5"})])],"derivedFrom":makeQuery(id+"F4.opExtrude","CAP_EDGE",EDGE,{"disambiguationData":[OSD([subQ3])],"isStart":false})});}
            var Q44;
            {var subQ1=sQuery(id+"F0.wireOp",EDGE,"E11");var subQ3=sQuery(id+"F3.wireOp",EDGE,"E15");Q44=makeQuery(id+"F4.boolean.opBoolean","SPLIT",EDGE,{"disambiguationData":[TD([makeQuery(id+"F2.opPattern","COPY",FACE,{"derivedFrom":makeQuery(id+"F1.opExtrude","SWEPT_FACE",FACE,{"disambiguationData":[OSD([subQ1])]}),"instanceName":"6"})])],"derivedFrom":makeQuery(id+"F4.opExtrude","CAP_EDGE",EDGE,{"disambiguationData":[OSD([subQ3])],"isStart":false})});}
            var Q45;
            {var subQ1=sQuery(id+"F0.wireOp",EDGE,"E11");var subQ3=sQuery(id+"F3.wireOp",EDGE,"E15");Q45=makeQuery(id+"F4.boolean.opBoolean","SPLIT",EDGE,{"disambiguationData":[TD([makeQuery(id+"F2.opPattern","COPY",FACE,{"derivedFrom":makeQuery(id+"F1.opExtrude","SWEPT_FACE",FACE,{"disambiguationData":[OSD([subQ1])]}),"instanceName":"7"})])],"derivedFrom":makeQuery(id+"F4.opExtrude","CAP_EDGE",EDGE,{"disambiguationData":[OSD([subQ3])],"isStart":false})});}
            var Q46;
            {var subQ1=sQuery(id+"F0.wireOp",EDGE,"E11");var subQ3=sQuery(id+"F3.wireOp",EDGE,"E15");Q46=makeQuery(id+"F4.boolean.opBoolean","SPLIT",EDGE,{"disambiguationData":[TD([makeQuery(id+"F2.opPattern","COPY",FACE,{"derivedFrom":makeQuery(id+"F1.opExtrude","SWEPT_FACE",FACE,{"disambiguationData":[OSD([subQ1])]}),"instanceName":"8"})])],"derivedFrom":makeQuery(id+"F4.opExtrude","CAP_EDGE",EDGE,{"disambiguationData":[OSD([subQ3])],"isStart":false})});}
            var Q47;
            {var subQ1=sQuery(id+"F0.wireOp",EDGE,"E11");var subQ3=sQuery(id+"F3.wireOp",EDGE,"E15");Q47=makeQuery(id+"F4.boolean.opBoolean","SPLIT",EDGE,{"disambiguationData":[TD([makeQuery(id+"F2.opPattern","COPY",FACE,{"derivedFrom":makeQuery(id+"F1.opExtrude","SWEPT_FACE",FACE,{"disambiguationData":[OSD([subQ1])]}),"instanceName":"9"})])],"derivedFrom":makeQuery(id+"F4.opExtrude","CAP_EDGE",EDGE,{"disambiguationData":[OSD([subQ3])],"isStart":false})});}
            fillet(context, id + "F9", {"entities" : qUnion([Q0, Q1, Q2, Q3, Q4, Q5, Q6, Q7, Q8, Q9, Q10, Q11, Q12, Q13, Q14, Q15, Q16, Q17, Q18, Q19, Q20, Q21, Q22, Q23, Q24, Q25, Q26, Q27, Q28, Q29, Q30, Q31, Q32, Q33, Q34, Q35, Q36, Q37, Q38, Q39, Q40, Q41, Q42, Q43, Q44, Q45, Q46, Q47]), "radius" : 5.08 * mm, "tangentPropagation" : true, "allowEdgeOverflow" : false});
        }
    });
